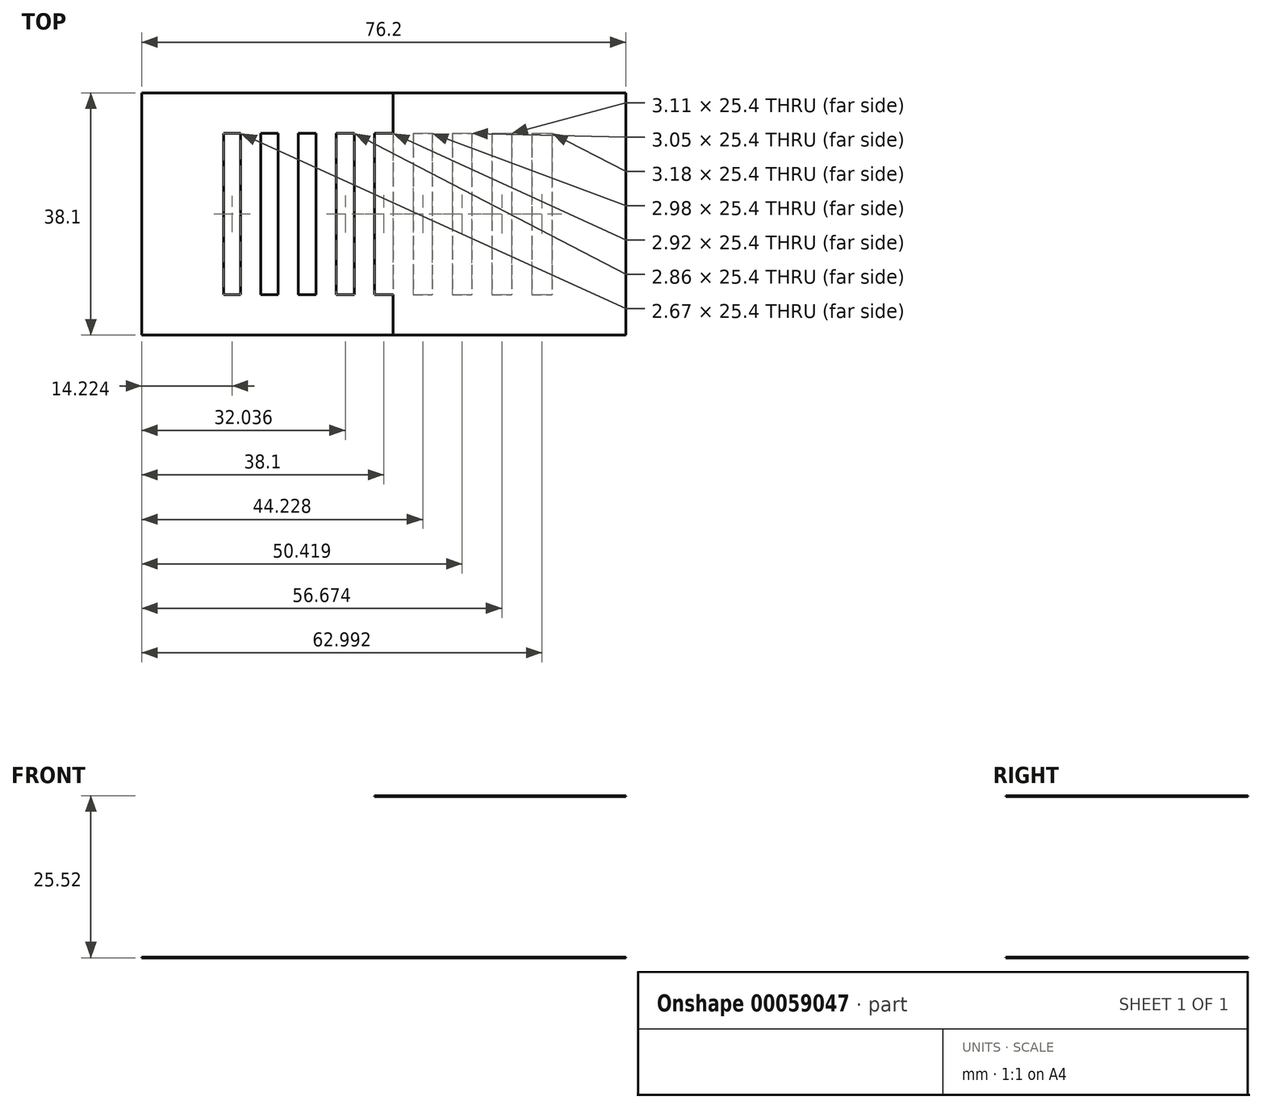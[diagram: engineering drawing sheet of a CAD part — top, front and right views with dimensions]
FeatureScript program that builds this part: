
annotation { "Feature Type Name" : "Feature", "Feature Type Description" : "" }
export const myFeature = defineFeature(function(context is Context, id is Id, definition is map)
    precondition{}
    {
        {
            assignVariable(context, id + "F0", {"name" : "MAT", "anyValue" : .125});
        }
        {
            var Q0;
            Q0=qCreatedBy(makeId("Top.planeOp"),FACE);
            var sketch = newSketch(context, id + "F1", { "sketchPlane" : qUnion([Q0])});
            skLineSegment(sketch, "E0.rect.bottom", {"start": v(-38.1, 19.05) * mm, "end": v(38.1, 19.05) * mm});
            skLineSegment(sketch, "E0.rect.top", {"start": v(-38.1, -19.05) * mm, "end": v(38.1, -19.05) * mm});
            skLineSegment(sketch, "E0.rect.left", {"start": v(-38.1, 19.05) * mm, "end": v(-38.1, -19.05) * mm});
            skLineSegment(sketch, "E0.rect.right", {"start": v(38.1, 19.05) * mm, "end": v(38.1, -19.05) * mm});
            skPoint(sketch, "E0.rect.middle", {"position": v(0, 0) * mm});
            skLineSegment(sketch, "E1.bottom", {"start": v(-25.2, 12.7) * mm, "end": v(-22.54, 12.7) * mm});
            skLineSegment(sketch, "E1.top", {"start": v(-25.2, -12.7) * mm, "end": v(-22.54, -12.7) * mm});
            skLineSegment(sketch, "E1.left", {"start": v(-25.2, 12.7) * mm, "end": v(-25.2, -12.7) * mm});
            skLineSegment(sketch, "E1.right", {"start": v(-22.54, 12.7) * mm, "end": v(-22.54, -12.7) * mm});
            skLineSegment(sketch, "E2.bottom", {"start": v(-7.5, 12.7) * mm, "end": v(-4.64, 12.7) * mm});
            skLineSegment(sketch, "E2.top", {"start": v(-7.5, -12.7) * mm, "end": v(-4.64, -12.7) * mm});
            skLineSegment(sketch, "E2.left", {"start": v(-7.5, 12.7) * mm, "end": v(-7.5, -12.7) * mm});
            skLineSegment(sketch, "E2.right", {"start": v(-4.64, 12.7) * mm, "end": v(-4.64, -12.7) * mm});
            skLineSegment(sketch, "E3.bottom", {"start": v(-1.46, 12.7) * mm, "end": v(1.46, 12.7) * mm});
            skLineSegment(sketch, "E3.top", {"start": v(-1.46, -12.7) * mm, "end": v(1.46, -12.7) * mm});
            skLineSegment(sketch, "E3.left", {"start": v(-1.46, 12.7) * mm, "end": v(-1.46, -12.7) * mm});
            skLineSegment(sketch, "E3.right", {"start": v(1.46, 12.7) * mm, "end": v(1.46, -12.7) * mm});
            skLineSegment(sketch, "E4.bottom", {"start": v(4.64, 12.7) * mm, "end": v(7.62, 12.7) * mm});
            skLineSegment(sketch, "E4.top", {"start": v(4.64, -12.7) * mm, "end": v(7.62, -12.7) * mm});
            skLineSegment(sketch, "E4.left", {"start": v(4.64, 12.7) * mm, "end": v(4.64, -12.7) * mm});
            skLineSegment(sketch, "E4.right", {"start": v(7.62, 12.7) * mm, "end": v(7.62, -12.7) * mm});
            skLineSegment(sketch, "E5.bottom", {"start": v(23.3, 12.7) * mm, "end": v(26.48, 12.7) * mm});
            skLineSegment(sketch, "E5.top", {"start": v(23.3, -12.7) * mm, "end": v(26.48, -12.7) * mm});
            skLineSegment(sketch, "E5.left", {"start": v(23.3, 12.7) * mm, "end": v(23.3, -12.7) * mm});
            skLineSegment(sketch, "E5.right", {"start": v(26.48, 12.7) * mm, "end": v(26.48, -12.7) * mm});
            skPoint(sketch, "E6", {"position": v(0, 12.7) * mm});
            skLineSegment(sketch, "E7.bottom", {"start": v(10.8, 12.7) * mm, "end": v(13.84, 12.7) * mm});
            skLineSegment(sketch, "E7.top", {"start": v(10.8, -12.7) * mm, "end": v(13.84, -12.7) * mm});
            skLineSegment(sketch, "E7.left", {"start": v(10.8, 12.7) * mm, "end": v(10.8, -12.7) * mm});
            skLineSegment(sketch, "E7.right", {"start": v(13.84, 12.7) * mm, "end": v(13.84, -12.7) * mm});
            skLineSegment(sketch, "E8.bottom", {"start": v(17.02, 12.7) * mm, "end": v(20.13, 12.7) * mm});
            skLineSegment(sketch, "E8.top", {"start": v(17.02, -12.7) * mm, "end": v(20.13, -12.7) * mm});
            skLineSegment(sketch, "E8.left", {"start": v(17.02, 12.7) * mm, "end": v(17.02, -12.7) * mm});
            skLineSegment(sketch, "E8.right", {"start": v(20.13, 12.7) * mm, "end": v(20.13, -12.7) * mm});
            skLineSegment(sketch, "E9.bottom", {"start": v(-10.67, 12.7) * mm, "end": v(-13.46, 12.7) * mm});
            skLineSegment(sketch, "E9.top", {"start": v(-10.67, -12.7) * mm, "end": v(-13.46, -12.7) * mm});
            skLineSegment(sketch, "E9.left", {"start": v(-10.67, 12.7) * mm, "end": v(-10.67, -12.7) * mm});
            skLineSegment(sketch, "E9.right", {"start": v(-13.46, 12.7) * mm, "end": v(-13.46, -12.7) * mm});
            skLineSegment(sketch, "E10.bottom", {"start": v(-16.64, 12.7) * mm, "end": v(-19.37, 12.7) * mm});
            skLineSegment(sketch, "E10.top", {"start": v(-16.64, -12.7) * mm, "end": v(-19.37, -12.7) * mm});
            skLineSegment(sketch, "E10.left", {"start": v(-16.64, 12.7) * mm, "end": v(-16.64, -12.7) * mm});
            skLineSegment(sketch, "E10.right", {"start": v(-19.37, 12.7) * mm, "end": v(-19.37, -12.7) * mm});
            skSolve(sketch);
        }
        {
            var Q0;
            Q0 = qSketchRegion(id + "F1", true);
            extrude(context, id + "F2", {"entities" : qUnion([Q0]), "depth" : (getVariable(context, 'MAT')) * mm});
        }
        {
            var Q0;
            Q0=qCreatedBy(makeId("Top.planeOp"),FACE);
            cPlane(context, id + "F3", {"entities" : qUnion([Q0]), "cplaneType" : CPlaneType.OFFSET, "offset" : 25.4 * mm, "width" : 152.4 * mm, "height" : 152.4 * mm});
        }
        {
            var Q0;
            Q0=qCreatedBy(id+"F3.planeOp",FACE);
            var sketch = newSketch(context, id + "F4", { "sketchPlane" : qUnion([Q0])});
            skLineSegment(sketch, "E11.0", {"start": v(-1.46, 12.7) * mm, "end": v(1.46, 12.7) * mm});
            skLineSegment(sketch, "E12.0", {"start": v(-1.46, -12.7) * mm, "end": v(1.46, -12.7) * mm});
            skLineSegment(sketch, "E13.0", {"start": v(-1.46, 12.7) * mm, "end": v(-1.46, -12.7) * mm});
            skLineSegment(sketch, "E14.0", {"start": v(-38.1, 19.05) * mm, "end": v(38.1, 19.05) * mm});
            skLineSegment(sketch, "E15.0", {"start": v(-38.1, -19.05) * mm, "end": v(38.1, -19.05) * mm});
            skLineSegment(sketch, "E16", {"start": v(1.46, 12.7) * mm, "end": v(1.46, 19.05) * mm});
            skLineSegment(sketch, "E17", {"start": v(1.46, -12.7) * mm, "end": v(1.46, -19.05) * mm});
            skLineSegment(sketch, "E18.0", {"start": v(38.1, 19.05) * mm, "end": v(38.1, -19.05) * mm});
            skSolve(sketch);
        }
        {
            var Q0;
            Q0 = qSketchRegion(id + "F4", true);
            extrude(context, id + "F5", {"entities" : qUnion([Q0]), "depth" : (getVariable(context, 'MAT')) * mm});
        }
    });
